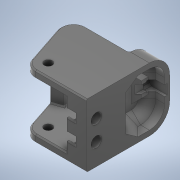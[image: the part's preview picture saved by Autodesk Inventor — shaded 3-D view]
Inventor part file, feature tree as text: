
AUTODESK INVENTOR PART (.ipt)
format: ipt  version: 2020 (Build 240168000, 168)  size: 1,040,896 bytes
history: native  units: mm
features: extrude x12, sketch x12, chamfer x7, fillet x3
ambient origin geometry x8: Origin, YZ Plane, XZ Plane, XY Plane, X Axis, Y Axis, Z Axis, Center Point
bodies: Volumenkörper1 (feature_tree)
feature tree (34):
  extrude  "Extrusion1"  Depth=20.0mm
  extrude  "Extrusion2"  Depth=8.0mm
  fillet  "Rundung1"  Radius=8.0mm
  extrude  "Extrusion3"  Depth=25.0mm
  extrude  "Extrusion5"  Depth=3.0mm
  extrude  "Extrusion6"  TaperAngle=0.0deg  [1 undecoded]
  chamfer  "Fase2"  Distance=7.0mm
  extrude  "Extrusion4"  Depth=4.2mm
  extrude  "Extrusion7"  TaperAngle=0.0deg  [1 undecoded]
  extrude  "Extrusion9"  Depth=10.0mm TaperAngle=0.0deg
  fillet  "Rundung2"  Radius=2.5mm
  extrude  "Extrusion10"  Depth=10.0mm TaperAngle=0.0deg
  chamfer  "Fase7"  Distance=4.0mm
  extrude  "Extrusion11"  Depth=10.0mm
  extrude  "Extrusion12"  Depth=10.0mm
  chamfer  "Fase9"  Distance=0.5mm
  chamfer  "Fase10"  Distance=7.0mm
  chamfer  "Fase11"  Distance=4.0mm
  extrude  "Extrusion13"  Depth=10.0mm
  chamfer  "Fase12"  Distance=4.0mm
  fillet  "Rundung3"  Radius=3.2mm
  chamfer  "Fase13"  Distance=1.0mm
  sketch  "Skizze1"  dims[d0=3.2mm d1=20.0mm]
  sketch  "Skizze2"  dims[d2=25.0mm d3=8.0mm d4=8.0mm]
  sketch  "Skizze3"  dims[d5=5.0mm d6=25.0mm]
  sketch  "Skizze4"  dims[d7=25.0mm d8=0.0mm d9=3.0mm]
  sketch  "Skizze6"  dims[d10=3.0mm d11=0.0mm d12=0.0mm]
  sketch  "Skizze7"  dims[d13=25.0mm]
  sketch  "Skizze8"  dims[d14=8.0mm]
  sketch  "Skizze10"  dims[d15=2.0mm]
  sketch  "Skizze11"  dims[d16=12.0mm d17=7.0mm d18=0.0mm]
  sketch  "Skizze12"  dims[d22=0.5mm d23=2.0mm d24=45.0deg d25=4.2mm]
  sketch  "Skizze14"  dims[d26=8.0mm d27=0.0mm d28=0.0mm]
  sketch  "Skizze15"  dims[d33=5.0mm d34=10.0mm d35=0.0mm d36=2.5mm d37=10.0mm d38=0.0mm d39=4.0mm d40=15.2mm d41=15.0mm d42=0.5mm d43=0.0mm d53=7.0mm d54=4.0mm d55=0.0mm d56=0.5mm d60=4.0mm d61=3.2mm d62=1.0mm d63=10.0mm d64=0.0mm d65=0.75mm d66=2.0mm d67=45.0deg d68=2.0mm d69=1.0mm d70=2.2mm d71=0.0mm d72=3.2mm d73=0.7mm d74=2.0mm d75=2.0mm d76=0.0mm d80=3.5mm d81=2.0mm d82=45.0deg d83=3.5mm d84=2.0mm d85=45.0deg d86=2.0mm d87=2.0mm d88=45.0deg d89=2.0mm d90=0.0mm d91=0.5mm d92=2.0mm d93=45.0deg d94=1.0mm d95=1.0mm d96=2.0mm d97=45.0deg]
note: 2 required parameter values undecoded (feature->parameter linkage not recoverable at this tier; creation-order binding heuristic only, values carry confidence <= 0.55)
